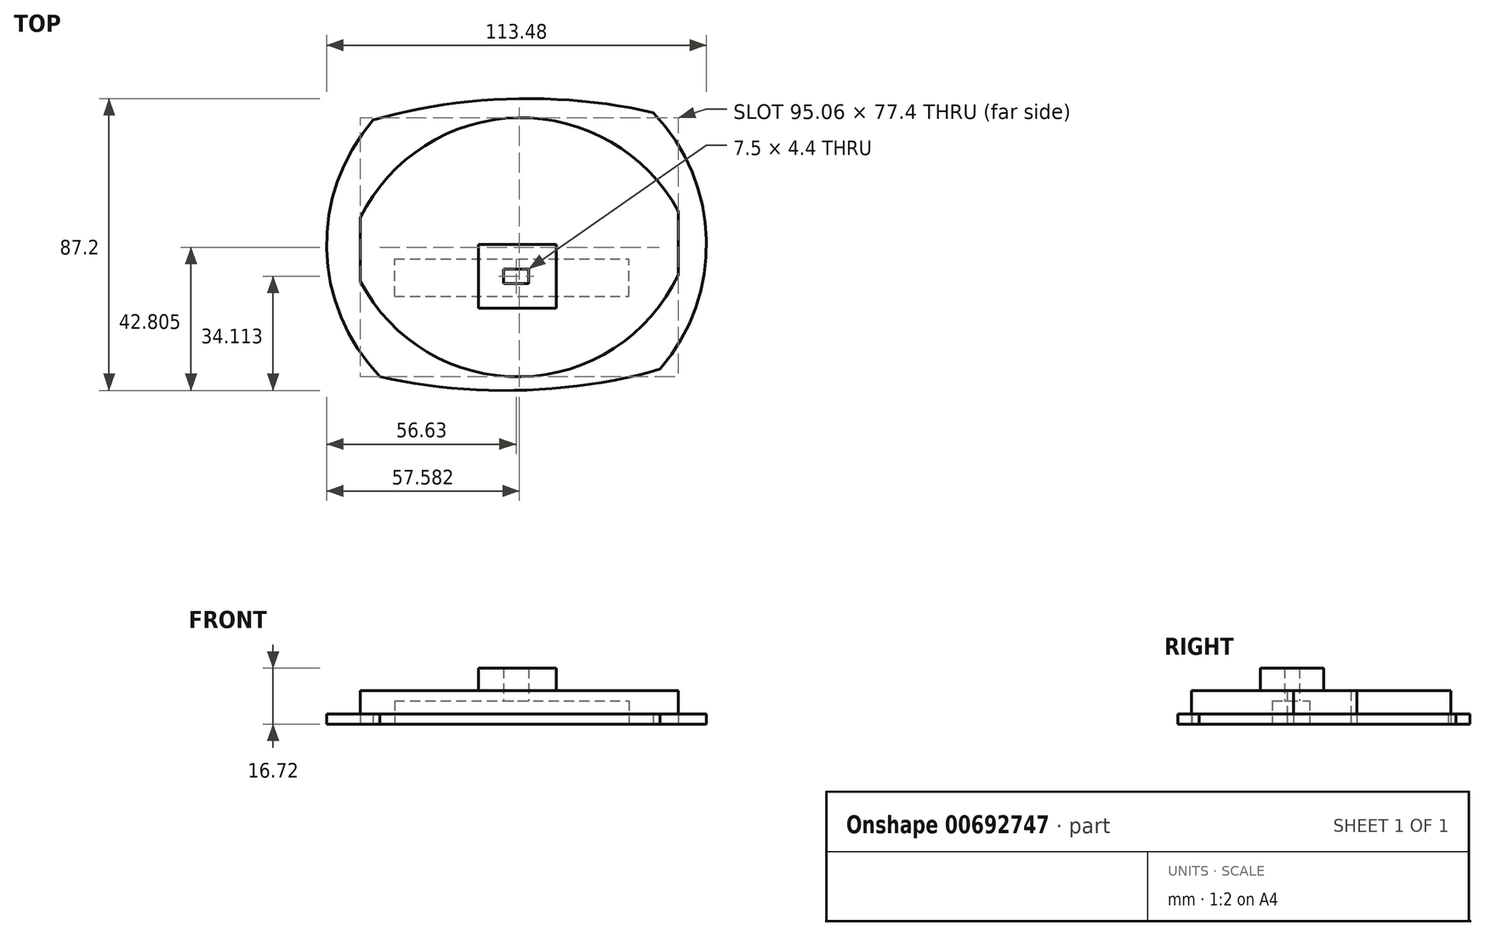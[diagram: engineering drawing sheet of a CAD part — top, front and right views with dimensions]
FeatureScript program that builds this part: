
annotation { "Feature Type Name" : "Feature", "Feature Type Description" : "" }
export const myFeature = defineFeature(function(context is Context, id is Id, definition is map)
    precondition{}
    {
        {
            var Q0;
            Q0=qCreatedBy(makeId("Top.planeOp"),FACE);
            var sketch = newSketch(context, id + "F0", { "sketchPlane" : qUnion([Q0])});
            skLineSegment(sketch, "E0.left", {"start": v(-46.64, 8.05) * mm, "end": v(-46.69, -10.95) * mm});
            skLineSegment(sketch, "E0.right", {"start": v(48.37, 9.9) * mm, "end": v(48.32, -9.1) * mm});
            skPoint(sketch, "E1.endSnap0", {"position": v(0, -24.76) * mm});
            skArc(sketch, "E2", {"start": v(48.37, 9.9) * mm, "mid": v(0.3, 37.9) * mm, "end": v(-46.64, 8.05) * mm});
            skArc(sketch, "E3", {"start": v(-46.69, -10.95) * mm, "mid": v(1.4, -39.5) * mm, "end": v(48.32, -9.1) * mm});
            skPoint(sketch, "E1.end.orphan", {"position": v(0, -39.5) * mm});
            skEllipticalArc(sketch, "E4", {});
            skEllipticalArc(sketch, "E5.trimOffspring", {});
            skPoint(sketch, "E6.start.orphan", {"position": v(0.3, 37.9) * mm});
            skArc(sketch, "E7", {"start": v(42.85, -37.2) * mm, "mid": v(56.72, 1.52) * mm, "end": v(40.8, 39.43) * mm});
            skArc(sketch, "E8.trimOffspring", {"start": v(-42.85, 37.2) * mm, "mid": v(-56.72, -1.52) * mm, "end": v(-40.8, -39.43) * mm});
            const initialGuessF0  = {"E4": [0, 0, 0.9996431337373777, 0.02671338937153828, 0.0880768689629508, 0.04355424366850744, 4.217423522181871, 5.207354438587494], "E5.trimOffspring": [0, 0, 0.9996431337373777, 0.02671338937153828, 0.0880768689629508, 0.04355424366850744, 1.0758308685920797, 2.065761784997701]};
            skSetInitialGuess(sketch, initialGuessF0);
            skSolve(sketch);
        }
        {
            var Q0;
            Q0=makeQuery(id+"F0.imprint","IMPRINT",FACE,{"disambiguationData":[TD([[makeQuery(id+"F0.imprint","IMPRINT",EDGE,{"derivedFrom":sQuery(id+"F0.wireOp",EDGE,"E0.left")}),1.0]])]});
            extrude(context, id + "F1", {"entities" : qUnion([Q0]), "depth" : 10 * mm, "offsetDistance" : 25 * mm});
        }
        {
            var Q0;
            Q0=makeQuery(id+"F0.imprint","IMPRINT",FACE,{"disambiguationData":[TD([[makeQuery(id+"F0.imprint","IMPRINT",EDGE,{"derivedFrom":sQuery(id+"F0.wireOp",EDGE,"E0.left")}),-1.0]])]});
            extrude(context, id + "F2", {"entities" : qUnion([Q0]), "depth" : 3 * mm, "offsetDistance" : 25 * mm});
        }
        {
            var Q0;
            {var subQ0=sQuery(id+"F0.wireOp",EDGE,"779bcca1-b2ed-4fb6-bc24-04eba6e0b783");var subQ1=sQuery(id+"F0.wireOp",EDGE,"26bc1371-ee27-41cd-9060-f189532f9eb9");var subQ2=sQuery(id+"F0.wireOp",EDGE,"E0.right");var subQ3=sQuery(id+"F0.wireOp",EDGE,"E0.left");Q0=makeQuery(id+"F2.boolean.opBoolean","MERGE",FACE,{"derivedFrom":[makeQuery(id+"F1.opExtrude","CAP_FACE",FACE,{"disambiguationData":[OSD([subQ3,subQ2,subQ1,subQ0])],"isStart":true}),makeQuery(id+"F2.opExtrude","CAP_FACE",FACE,{"disambiguationData":[OSD([subQ3,subQ2,subQ1,subQ0,sQuery(id+"F0.wireOp",EDGE,"wsJQ3WIa-Jgsx-jDmX-L3gV-xdBJbMgAOQ1R")])],"isStart":true})]});}
            var sketch = newSketch(context, id + "F3", { "sketchPlane" : qUnion([Q0])});
            skLineSegment(sketch, "E9.bottom", {"start": v(-36.43, 15.42) * mm, "end": v(33.57, 15.42) * mm});
            skLineSegment(sketch, "E9.top", {"start": v(-36.43, 4.22) * mm, "end": v(33.57, 4.22) * mm});
            skLineSegment(sketch, "E9.left", {"start": v(-36.43, 15.42) * mm, "end": v(-36.43, 4.22) * mm});
            skLineSegment(sketch, "E9.right", {"start": v(33.57, 15.42) * mm, "end": v(33.57, 4.22) * mm});
            skSolve(sketch);
        }
        {
            var Q0;
            Q0 = qSketchRegion(id + "F3", true);
            extrude(context, id + "F4", {"entities" : qUnion([Q0]), "operationType" : NewBodyOperationType.REMOVE, "oppositeDirection" : true, "depth" : 7 * mm, "offsetDistance" : 25 * mm});
        }
        {
            var Q0;
            Q0=makeQuery(id+"F4.boolean.opBoolean","COPY",FACE,{"derivedFrom":makeQuery(id+"F4.opExtrude","CAP_FACE",FACE,{"disambiguationData":[OSD([sQuery(id+"F3.wireOp",EDGE,"E9.bottom"),sQuery(id+"F3.wireOp",EDGE,"E9.top"),sQuery(id+"F3.wireOp",EDGE,"E9.left"),sQuery(id+"F3.wireOp",EDGE,"E9.right")])],"isStart":false})});
            var sketch = newSketch(context, id + "F5", { "sketchPlane" : qUnion([Q0])});
            skLineSegment(sketch, "E10.bottom", {"start": v(-3.86, 11.69) * mm, "end": v(3.64, 11.69) * mm});
            skLineSegment(sketch, "E10.top", {"start": v(-3.86, 7.29) * mm, "end": v(3.64, 7.29) * mm});
            skLineSegment(sketch, "E10.left", {"start": v(-3.86, 11.69) * mm, "end": v(-3.86, 7.29) * mm});
            skLineSegment(sketch, "E10.right", {"start": v(3.64, 11.69) * mm, "end": v(3.64, 7.29) * mm});
            skLineSegment(sketch, "E11.bottom", {"start": v(-11.4, 0) * mm, "end": v(11.9, 0) * mm});
            skLineSegment(sketch, "E11.top", {"start": v(-11.4, 18.95) * mm, "end": v(11.9, 18.95) * mm});
            skLineSegment(sketch, "E11.left", {"start": v(-11.4, 0) * mm, "end": v(-11.4, 18.95) * mm});
            skLineSegment(sketch, "E11.right", {"start": v(11.9, 0) * mm, "end": v(11.9, 18.95) * mm});
            skSolve(sketch);
        }
        {
            var Q0;
            Q0 = qSketchRegion(id + "F5", true);
            extrude(context, id + "F6", {"entities" : qUnion([Q0]), "operationType" : NewBodyOperationType.ADD, "oppositeDirection" : true, "depth" : 9.72 * mm, "offsetDistance" : 25 * mm});
        }
        {
            var Q0;
            Q0=makeQuery(id+"F6.boolean.opBoolean","SPLIT",FACE,{"disambiguationData":[TD([makeQuery(id+"F6.opExtrude","SWEPT_FACE",FACE,{"disambiguationData":[OSD([sQuery(id+"F5.wireOp",EDGE,"E10.bottom")])]})])],"derivedFrom":makeQuery(id+"F1.opExtrude","CAP_FACE",FACE,{"disambiguationData":[OSD([sQuery(id+"F0.wireOp",EDGE,"E0.left"),sQuery(id+"F0.wireOp",EDGE,"E0.right"),sQuery(id+"F0.wireOp",EDGE,"E2"),sQuery(id+"F0.wireOp",EDGE,"E3")])],"isStart":false})});
            extrude(context, id + "F7", {"entities" : qUnion([Q0]), "operationType" : NewBodyOperationType.REMOVE, "oppositeDirection" : true, "depth" : 25 * mm, "offsetDistance" : 25 * mm});
        }
    });
